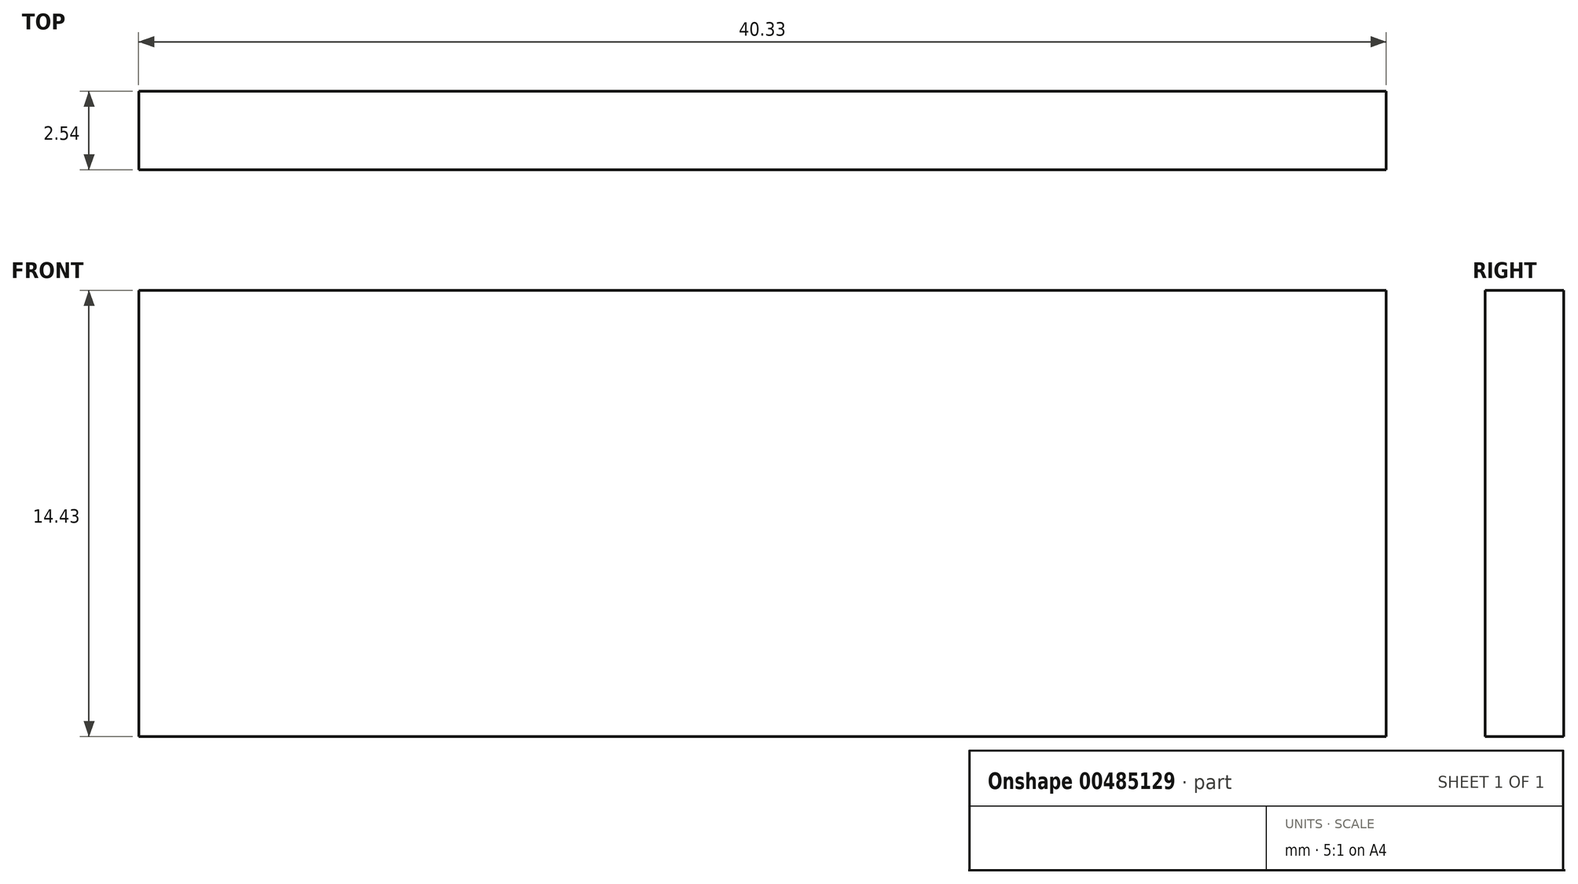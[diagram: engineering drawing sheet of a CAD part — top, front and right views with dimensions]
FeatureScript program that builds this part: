
annotation { "Feature Type Name" : "Feature", "Feature Type Description" : "" }
export const myFeature = defineFeature(function(context is Context, id is Id, definition is map)
    precondition{}
    {
        {
            var Q0;
            Q0=qCreatedBy(makeId("Front.planeOp"),FACE);
            var sketch = newSketch(context, id + "F0", { "sketchPlane" : qUnion([Q0])});
            skLineSegment(sketch, "E0.bottom", {"start": v(-161.29, -15.15) * mm, "end": v(-120.96, -15.15) * mm});
            skLineSegment(sketch, "E0.top", {"start": v(-161.29, -29.58) * mm, "end": v(-120.96, -29.58) * mm});
            skLineSegment(sketch, "E0.left", {"start": v(-161.29, -15.15) * mm, "end": v(-161.29, -29.58) * mm});
            skLineSegment(sketch, "E0.right", {"start": v(-120.96, -15.15) * mm, "end": v(-120.96, -29.58) * mm});
            skSolve(sketch);
        }
        {
            var Q0;
            Q0 = qSketchRegion(id + "F0", true);
            extrude(context, id + "F1", {"entities" : qUnion([Q0]), "depth" : 2.54 * mm});
        }
    });
